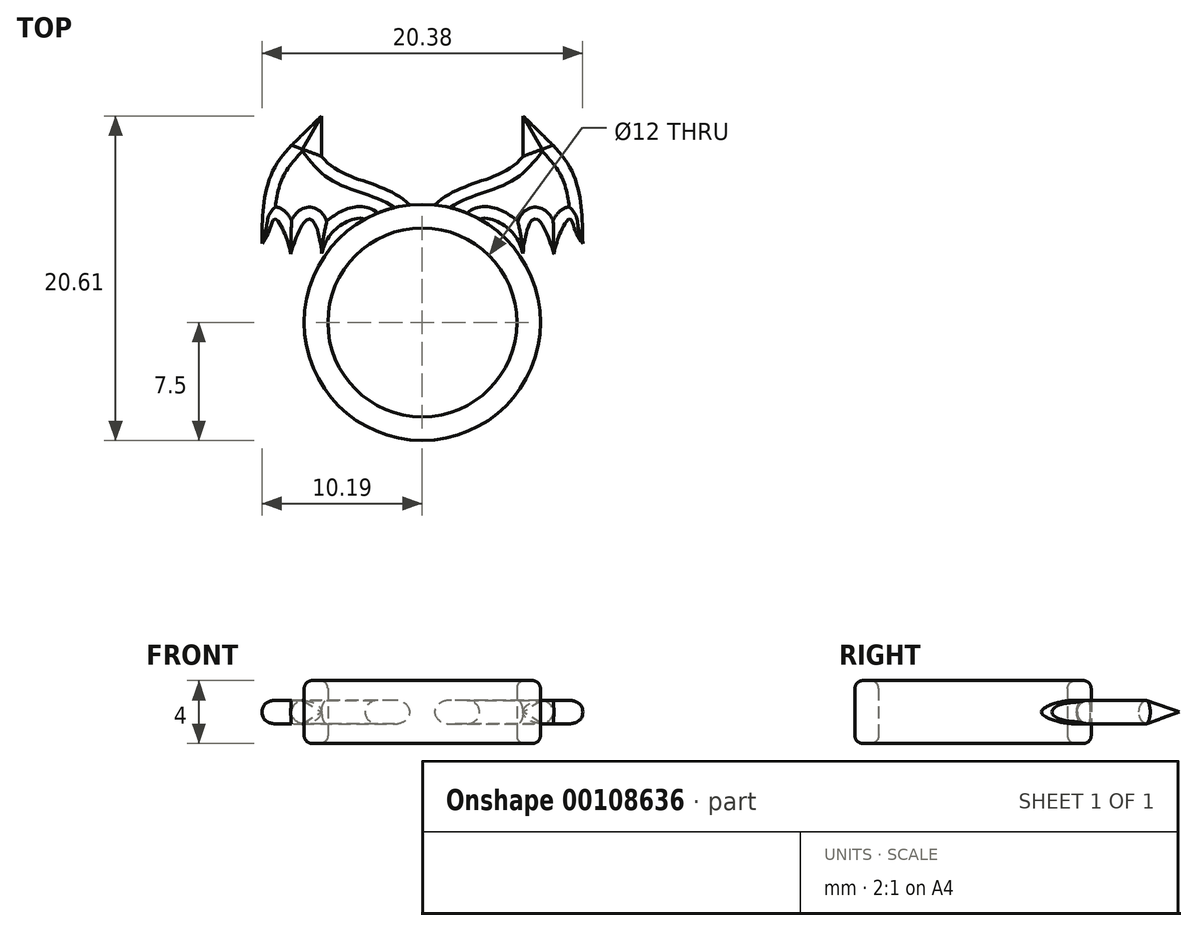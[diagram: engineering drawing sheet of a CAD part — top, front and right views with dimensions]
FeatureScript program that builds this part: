
annotation { "Feature Type Name" : "Feature", "Feature Type Description" : "" }
export const myFeature = defineFeature(function(context is Context, id is Id, definition is map)
    precondition{}
    {
        {
            var Q0;
            Q0=qCreatedBy(makeId("Top.planeOp"),FACE);
            var sketch = newSketch(context, id + "F0", { "sketchPlane" : qUnion([Q0])});
            skCircle(sketch, "E0", {"center": v(0, 0) * mm, "radius": 6 * mm});
            skCircle(sketch, "E1", {"center": v(0, 0) * mm, "radius": 7.5 * mm});
            skPoint(sketch, "E2", {"position": v(-4.26, 9.97) * mm});
            skPoint(sketch, "E3.MirrorP", {"position": v(4.26, 9.97) * mm});
            skSolve(sketch);
        }
        {
            var Q0;
            Q0=qSketchRegion(id+"F0",true);
            extrude(context, id + "F1", {"entities" : qUnion([Q0]), "endBound" : BoundingType.SYMMETRIC, "depth" : 4 * mm});
        }
        {
            var Q0;
            Q0=makeQuery(id+"F1.opExtrude","CAP_EDGE",EDGE,{"disambiguationData":[OSD([sQuery(id+"F0.wireOp",EDGE,"E0")])],"isStart":true});
            var Q1;
            Q1=makeQuery(id+"F1.opExtrude","CAP_EDGE",EDGE,{"disambiguationData":[OSD([sQuery(id+"F0.wireOp",EDGE,"E0")])],"isStart":false});
            var Q2;
            Q2=makeQuery(id+"F1.opExtrude","CAP_EDGE",EDGE,{"disambiguationData":[OSD([sQuery(id+"F0.wireOp",EDGE,"E1")])],"isStart":false});
            var Q3;
            Q3=makeQuery(id+"F1.opExtrude","CAP_EDGE",EDGE,{"disambiguationData":[OSD([sQuery(id+"F0.wireOp",EDGE,"E1")])],"isStart":true});
            fillet(context, id + "F2", {"entities" : qUnion([Q0, Q1, Q2, Q3]), "radius" : 0.5 * mm, "tangentPropagation" : true, "allowEdgeOverflow" : false});
        }
        {
            var Q0;
            Q0=makeQuery(id+"F0.imprint","IMPRINT",FACE,{"disambiguationData":[TD([[makeQuery(id+"F0.imprint","IMPRINT",EDGE,{"derivedFrom":sQuery(id+"F0.wireOp",EDGE,"E0")}),1.0]])]});
            extrude(context, id + "F3", {"entities" : qUnion([Q0]), "operationType" : NewBodyOperationType.REMOVE, "endBound" : BoundingType.SYMMETRIC, "oppositeDirection" : true, "depth" : 5 * mm});
        }
        {
            var Q0;
            Q0=qCreatedBy(makeId("Top.planeOp"),FACE);
            var sketch = newSketch(context, id + "F4", { "sketchPlane" : qUnion([Q0])});
            skFitSpline(sketch, "E4", {"points": [v(0.39, 7) * mm, v(5.37, 9.67) * mm, v(6.98, 11.9) * mm, v(6.4, 13.11) * mm], "startDerivative": vector(8.13, 11.1) * mm, "endDerivative": vector(-4.43, 4.6) * mm});
            skFitSpline(sketch, "E5", {"points": [v(6.4, 13.11) * mm, v(7.63, 11.93) * mm, v(9.2, 10.14) * mm, v(10.2, 5.02) * mm], "startDerivative": vector(5.35, -4.7) * mm, "endDerivative": vector(0.06, -19.28) * mm});
            skFitSpline(sketch, "E6", {"points": [v(10.2, 5.02) * mm, v(9.37, 6.58) * mm, v(8.36, 4.36) * mm], "startDerivative": vector(-4.07, 4.75) * mm, "endDerivative": vector(-1.11, -5.99) * mm});
            skFitSpline(sketch, "E7", {"points": [v(8.36, 4.36) * mm, v(7.15, 6.57) * mm, v(6.39, 4.38) * mm], "startDerivative": vector(-2.37, 7.92) * mm, "endDerivative": vector(-0.8, -7.89) * mm});
            skFitSpline(sketch, "E8", {"points": [v(6.39, 4.38) * mm, v(5.39, 6.01) * mm, v(3.84, 6.6) * mm, v(2.93, 6.03) * mm], "startDerivative": vector(-1.46, 6.27) * mm, "endDerivative": vector(-2.98, -2.86) * mm});
            skLineSegment(sketch, "E9", {"start": v(0.39, 7) * mm, "end": v(2.93, 6.03) * mm});
            skFitSpline(sketch, "E10.MirrorCS", {"points": [v(-0.39, 7) * mm, v(-5.37, 9.67) * mm, v(-6.98, 11.9) * mm, v(-6.4, 13.11) * mm], "startDerivative": vector(-8.13, 11.1) * mm, "endDerivative": vector(4.43, 4.6) * mm});
            skFitSpline(sketch, "E11.MirrorCS", {"points": [v(-6.4, 13.11) * mm, v(-7.63, 11.93) * mm, v(-9.2, 10.14) * mm, v(-10.2, 5.02) * mm], "startDerivative": vector(-5.35, -4.7) * mm, "endDerivative": vector(-0.06, -19.28) * mm});
            skFitSpline(sketch, "E12.MirrorCS", {"points": [v(-8.36, 4.36) * mm, v(-7.15, 6.57) * mm, v(-6.39, 4.38) * mm], "startDerivative": vector(2.37, 7.92) * mm, "endDerivative": vector(0.8, -7.89) * mm});
            skLineSegment(sketch, "E13.MirrorCS", {"start": v(-0.39, 7) * mm, "end": v(-2.93, 6.03) * mm});
            skFitSpline(sketch, "E14.MirrorCS", {"points": [v(-10.2, 5.02) * mm, v(-9.37, 6.58) * mm, v(-8.36, 4.36) * mm], "startDerivative": vector(4.07, 4.75) * mm, "endDerivative": vector(1.11, -5.99) * mm});
            skFitSpline(sketch, "E15.MirrorCS", {"points": [v(-6.39, 4.38) * mm, v(-5.39, 6.01) * mm, v(-3.84, 6.6) * mm, v(-2.93, 6.03) * mm], "startDerivative": vector(1.46, 6.27) * mm, "endDerivative": vector(2.98, -2.86) * mm});
            skLineSegment(sketch, "E16", {"start": v(8.3, 11.25) * mm, "end": v(6.4, 10.54) * mm});
            skLineSegment(sketch, "E17.MirrorCS", {"start": v(-8.3, 11.25) * mm, "end": v(-6.4, 10.54) * mm});
            skSolve(sketch);
        }
        {
            var Q0;
            {var subQ0=sQuery(id+"F4.wireOp",EDGE,"E6");Q0=makeQuery(id+"F4.imprint","IMPRINT",FACE,{"disambiguationData":[TD([[makeQuery(id+"F4.imprint","IMPRINT",EDGE,{"derivedFrom":subQ0}),-1.0]])]});}
            var Q1;
            Q1=makeQuery(id+"F4.imprint","IMPRINT",FACE,{"disambiguationData":[TD([[makeQuery(id+"F4.imprint","IMPRINT",EDGE,{"derivedFrom":sQuery(id+"F4.wireOp",EDGE,"E12.MirrorCS")}),1.0]])]});
            extrude(context, id + "F5", {"entities" : qUnion([Q0, Q1]), "operationType" : NewBodyOperationType.ADD, "endBound" : BoundingType.SYMMETRIC, "depth" : 1.5 * mm});
        }
        {
            var Q0;
            Q0=makeQuery(id+"F5.opExtrude","CAP_EDGE",EDGE,{"disambiguationData":[OSD([sQuery(id+"F4.wireOp",EDGE,"E10.MirrorCS")])],"isStart":false});
            var Q1;
            Q1=makeQuery(id+"F5.opExtrude","CAP_EDGE",EDGE,{"disambiguationData":[OSD([sQuery(id+"F4.wireOp",EDGE,"E11.MirrorCS")])],"isStart":false});
            var Q2;
            Q2=makeQuery(id+"F5.opExtrude","CAP_EDGE",EDGE,{"disambiguationData":[OSD([sQuery(id+"F4.wireOp",EDGE,"E14.MirrorCS")])],"isStart":false});
            var Q3;
            Q3=makeQuery(id+"F5.opExtrude","CAP_EDGE",EDGE,{"disambiguationData":[OSD([sQuery(id+"F4.wireOp",EDGE,"E12.MirrorCS")])],"isStart":false});
            var Q4;
            Q4=makeQuery(id+"F5.opExtrude","CAP_EDGE",EDGE,{"disambiguationData":[OSD([sQuery(id+"F4.wireOp",EDGE,"E15.MirrorCS")])],"isStart":false});
            var Q5;
            Q5=makeQuery(id+"F5.opExtrude","CAP_EDGE",EDGE,{"disambiguationData":[OSD([sQuery(id+"F4.wireOp",EDGE,"E4")])],"isStart":false});
            var Q6;
            Q6=makeQuery(id+"F5.opExtrude","CAP_EDGE",EDGE,{"disambiguationData":[OSD([sQuery(id+"F4.wireOp",EDGE,"E5")])],"isStart":false});
            var Q7;
            Q7=makeQuery(id+"F5.opExtrude","CAP_EDGE",EDGE,{"disambiguationData":[OSD([sQuery(id+"F4.wireOp",EDGE,"E6")])],"isStart":false});
            var Q8;
            Q8=makeQuery(id+"F5.opExtrude","CAP_EDGE",EDGE,{"disambiguationData":[OSD([sQuery(id+"F4.wireOp",EDGE,"E7")])],"isStart":false});
            var Q9;
            Q9=makeQuery(id+"F5.opExtrude","CAP_EDGE",EDGE,{"disambiguationData":[OSD([sQuery(id+"F4.wireOp",EDGE,"E8")])],"isStart":false});
            var Q10;
            Q10=makeQuery(id+"F5.opExtrude","CAP_EDGE",EDGE,{"disambiguationData":[OSD([sQuery(id+"F4.wireOp",EDGE,"E5")])],"isStart":true});
            var Q11;
            Q11=makeQuery(id+"F5.opExtrude","CAP_EDGE",EDGE,{"disambiguationData":[OSD([sQuery(id+"F4.wireOp",EDGE,"E6")])],"isStart":true});
            var Q12;
            Q12=makeQuery(id+"F5.opExtrude","CAP_EDGE",EDGE,{"disambiguationData":[OSD([sQuery(id+"F4.wireOp",EDGE,"E7")])],"isStart":true});
            var Q13;
            Q13=makeQuery(id+"F5.opExtrude","CAP_EDGE",EDGE,{"disambiguationData":[OSD([sQuery(id+"F4.wireOp",EDGE,"E8")])],"isStart":true});
            var Q14;
            Q14=makeQuery(id+"F5.opExtrude","CAP_EDGE",EDGE,{"disambiguationData":[OSD([sQuery(id+"F4.wireOp",EDGE,"E11.MirrorCS")])],"isStart":true});
            var Q15;
            Q15=makeQuery(id+"F5.opExtrude","CAP_EDGE",EDGE,{"disambiguationData":[OSD([sQuery(id+"F4.wireOp",EDGE,"E14.MirrorCS")])],"isStart":true});
            var Q16;
            Q16=makeQuery(id+"F5.opExtrude","CAP_EDGE",EDGE,{"disambiguationData":[OSD([sQuery(id+"F4.wireOp",EDGE,"E12.MirrorCS")])],"isStart":true});
            var Q17;
            Q17=makeQuery(id+"F5.opExtrude","CAP_EDGE",EDGE,{"disambiguationData":[OSD([sQuery(id+"F4.wireOp",EDGE,"E15.MirrorCS")])],"isStart":true});
            var Q18;
            Q18=makeQuery(id+"F5.opExtrude","CAP_EDGE",EDGE,{"disambiguationData":[OSD([sQuery(id+"F4.wireOp",EDGE,"E10.MirrorCS")])],"isStart":true});
            var Q19;
            Q19=makeQuery(id+"F5.opExtrude","CAP_EDGE",EDGE,{"disambiguationData":[OSD([sQuery(id+"F4.wireOp",EDGE,"E4")])],"isStart":true});
            fillet(context, id + "F6", {"entities" : qUnion([Q0, Q1, Q2, Q3, Q4, Q5, Q6, Q7, Q8, Q9, Q10, Q11, Q12, Q13, Q14, Q15, Q16, Q17, Q18, Q19]), "radius" : 0.75 * mm, "tangentPropagation" : true, "allowEdgeOverflow" : false});
        }
        {
            var Q1;
            Q1=makeQuery(id+"F5.opExtrude","SWEPT_FACE",FACE,{"disambiguationData":[OSD([sQuery(id+"F4.wireOp",EDGE,"E17.MirrorCS")])]});
            var Q2;
            Q2=sQuery(id+"F4.wireOp",VERTEX,"E11.MirrorCS.start");
            loft(context, id + "F7", {"operationType" : NewBodyOperationType.ADD, "sheetProfilesArray" : [{ "sheetProfileEntities" : qUnion([Q1]) }, { "sheetProfileEntities" : qUnion([Q2]) }]});
        }
        {
            var Q1;
            Q1=makeQuery(id+"F5.opExtrude","SWEPT_FACE",FACE,{"disambiguationData":[OSD([sQuery(id+"F4.wireOp",EDGE,"E16")])]});
            var Q2;
            Q2=sQuery(id+"F4.wireOp",VERTEX,"E5.0.internal");
            loft(context, id + "F8", {"operationType" : NewBodyOperationType.ADD, "sheetProfilesArray" : [{ "sheetProfileEntities" : qUnion([Q1]) }, { "sheetProfileEntities" : qUnion([Q2]) }]});
        }
    });
